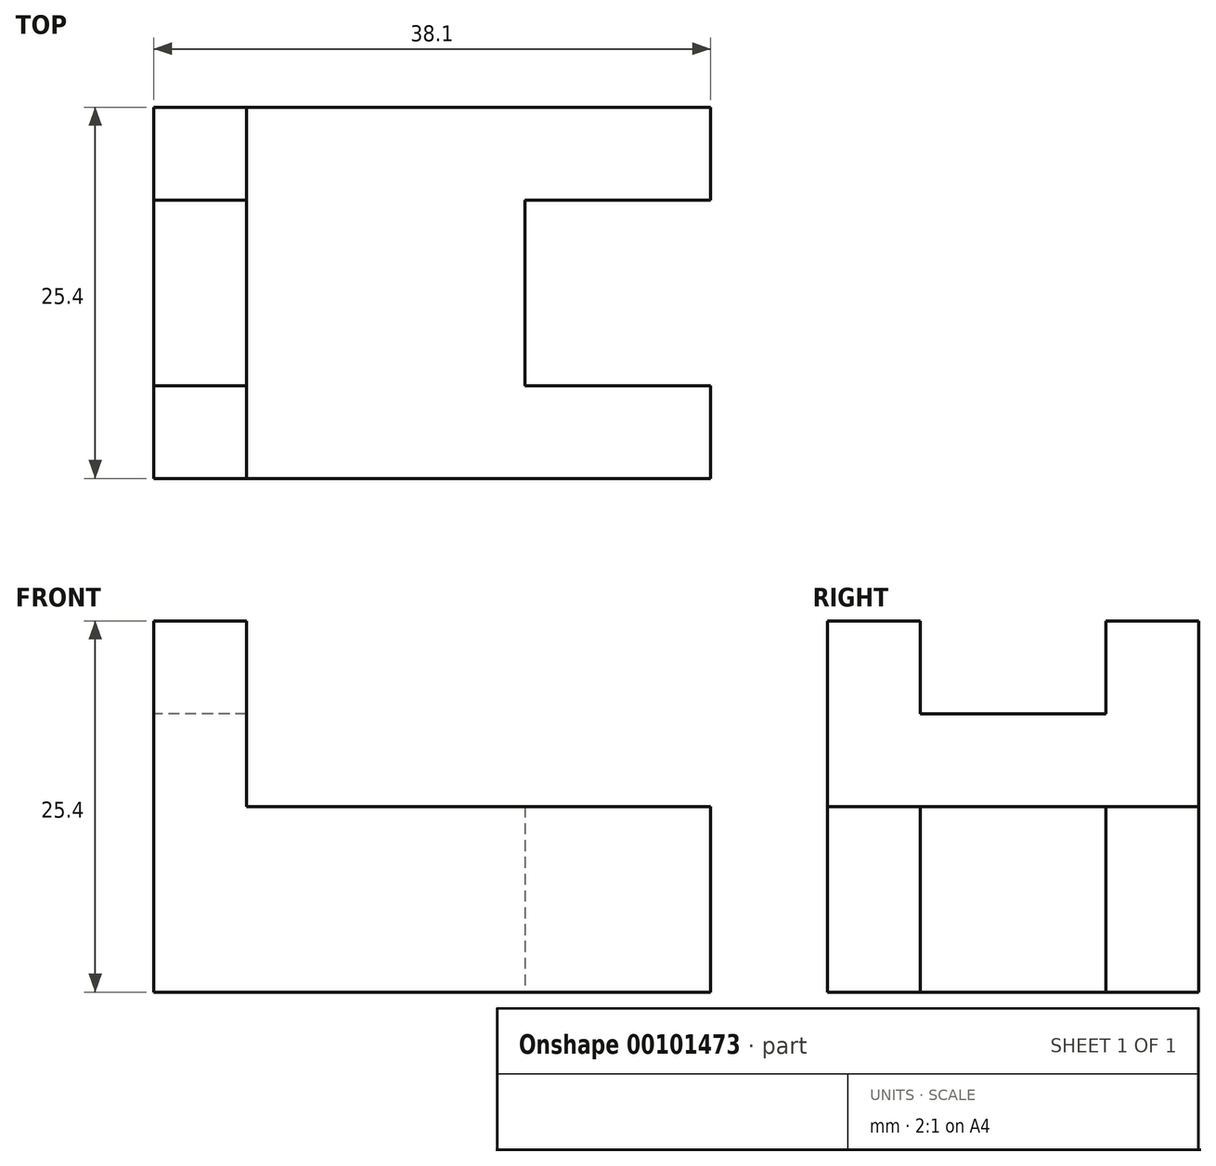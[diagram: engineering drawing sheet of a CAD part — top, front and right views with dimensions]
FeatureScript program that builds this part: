
annotation { "Feature Type Name" : "Feature", "Feature Type Description" : "" }
export const myFeature = defineFeature(function(context is Context, id is Id, definition is map)
    precondition{}
    {
        {
            var Q0;
            Q0=qCreatedBy(makeId("Top.planeOp"),FACE);
            var sketch = newSketch(context, id + "F0", { "sketchPlane" : qUnion([Q0])});
            skLineSegment(sketch, "E0", {"start": v(0, 0) * mm, "end": v(38.1, 0) * mm});
            skLineSegment(sketch, "E1", {"start": v(38.1, 0) * mm, "end": v(38.1, -6.35) * mm});
            skLineSegment(sketch, "E2", {"start": v(38.1, -6.35) * mm, "end": v(25.4, -6.35) * mm});
            skLineSegment(sketch, "E3", {"start": v(25.4, -6.35) * mm, "end": v(25.4, -19.05) * mm});
            skLineSegment(sketch, "E4", {"start": v(25.4, -19.05) * mm, "end": v(38.1, -19.05) * mm});
            skLineSegment(sketch, "E5", {"start": v(38.1, -19.05) * mm, "end": v(38.1, -25.4) * mm});
            skLineSegment(sketch, "E6", {"start": v(38.1, -25.4) * mm, "end": v(0, -25.4) * mm});
            skLineSegment(sketch, "E7", {"start": v(0, -25.4) * mm, "end": v(0, 0) * mm});
            skSolve(sketch);
        }
        {
            var Q0;
            Q0=makeQuery(id+"F0.imprint","IMPRINT",FACE,{"disambiguationData":[TD([[makeQuery(id+"F0.imprint","IMPRINT",EDGE,{"derivedFrom":sQuery(id+"F0.wireOp",EDGE,"E0")}),-1.0]])]});
            extrude(context, id + "F1", {"entities" : qUnion([Q0]), "depth" : 12.7 * mm});
        }
        {
            var Q0;
            Q0=qCreatedBy(makeId("Right.planeOp"),FACE);
            var sketch = newSketch(context, id + "F2", { "sketchPlane" : qUnion([Q0])});
            skLineSegment(sketch, "E8", {"start": v(0, 0) * mm, "end": v(0, 25.4) * mm});
            skLineSegment(sketch, "E9", {"start": v(0, 25.4) * mm, "end": v(-6.35, 25.4) * mm});
            skLineSegment(sketch, "E10", {"start": v(-6.35, 25.4) * mm, "end": v(-6.35, 19.05) * mm});
            skLineSegment(sketch, "E11", {"start": v(-6.35, 19.05) * mm, "end": v(-19.05, 19.05) * mm});
            skLineSegment(sketch, "E12", {"start": v(-19.05, 19.05) * mm, "end": v(-19.05, 25.4) * mm});
            skLineSegment(sketch, "E13", {"start": v(-19.05, 25.4) * mm, "end": v(-25.4, 25.4) * mm});
            skLineSegment(sketch, "E14", {"start": v(-25.4, 25.4) * mm, "end": v(-25.4, 0) * mm});
            skLineSegment(sketch, "E15", {"start": v(-25.4, 0) * mm, "end": v(0, 0) * mm});
            skSolve(sketch);
        }
        {
            var Q0;
            Q0=makeQuery(id+"F2.imprint","IMPRINT",FACE,{"disambiguationData":[TD([[makeQuery(id+"F2.imprint","IMPRINT",EDGE,{"derivedFrom":sQuery(id+"F2.wireOp",EDGE,"E8")}),1.0]])]});
            extrude(context, id + "F3", {"entities" : qUnion([Q0]), "operationType" : NewBodyOperationType.ADD, "depth" : 6.35 * mm});
        }
    });
